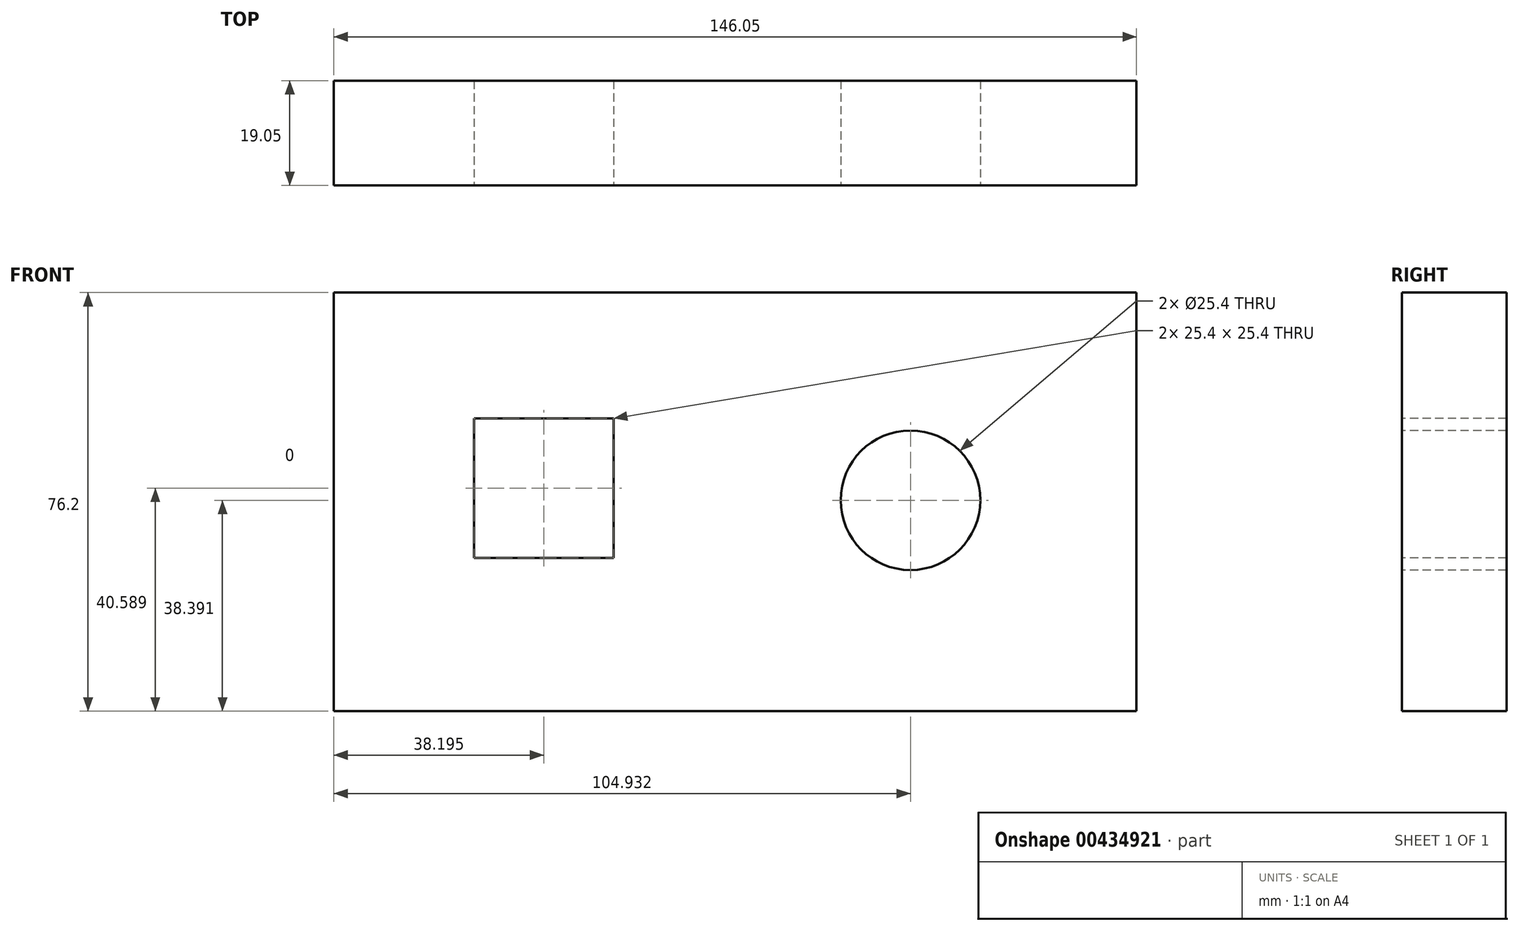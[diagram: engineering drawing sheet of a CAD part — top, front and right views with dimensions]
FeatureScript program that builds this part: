
annotation { "Feature Type Name" : "Feature", "Feature Type Description" : "" }
export const myFeature = defineFeature(function(context is Context, id is Id, definition is map)
    precondition{}
    {
        {
            var Q0;
            Q0=qCreatedBy(makeId("Front.planeOp"),FACE);
            var sketch = newSketch(context, id + "F0", { "sketchPlane" : qUnion([Q0])});
            skLineSegment(sketch, "E0", {"start": v(-76.38, 0) * mm, "end": v(69.67, 0) * mm});
            skLineSegment(sketch, "E1", {"start": v(69.67, 0) * mm, "end": v(69.67, -76.2) * mm});
            skLineSegment(sketch, "E2", {"start": v(69.67, -76.2) * mm, "end": v(-76.38, -76.2) * mm});
            skLineSegment(sketch, "E3", {"start": v(-76.38, -76.2) * mm, "end": v(-76.38, 0) * mm});
            skSolve(sketch);
        }
        {
            var Q0;
            Q0=makeQuery(id+"F0.imprint","IMPRINT",FACE,{"disambiguationData":[TD([[makeQuery(id+"F0.imprint","IMPRINT",EDGE,{"derivedFrom":sQuery(id+"F0.wireOp",EDGE,"E0")}),-1.0]])]});
            extrude(context, id + "F1", {"entities" : qUnion([Q0]), "depth" : 19.05 * mm});
        }
        {
            var Q0;
            Q0=makeQuery(id+"F1.opExtrude","CAP_FACE",FACE,{"disambiguationData":[OSD([sQuery(id+"F0.wireOp",EDGE,"E0"),sQuery(id+"F0.wireOp",EDGE,"E1"),sQuery(id+"F0.wireOp",EDGE,"E2"),sQuery(id+"F0.wireOp",EDGE,"E3")])],"isStart":false});
            var sketch = newSketch(context, id + "F2", { "sketchPlane" : qUnion([Q0])});
            skLineSegment(sketch, "E4", {"start": v(-50.88, -22.91) * mm, "end": v(-50.88, -48.31) * mm});
            skLineSegment(sketch, "E5", {"start": v(-50.88, -48.31) * mm, "end": v(-25.48, -48.31) * mm});
            skLineSegment(sketch, "E6", {"start": v(-25.48, -48.31) * mm, "end": v(-25.48, -22.91) * mm});
            skLineSegment(sketch, "E7", {"start": v(-25.48, -22.91) * mm, "end": v(-50.88, -22.91) * mm});
            skCircle(sketch, "E8", {"center": v(28.55, -37.8) * mm, "radius": 12.7 * mm});
            skSolve(sketch);
        }
        {
            var Q0;
            Q0=makeQuery(id+"F2.imprint","IMPRINT",FACE,{"disambiguationData":[TD([[makeQuery(id+"F2.imprint","IMPRINT",EDGE,{"derivedFrom":sQuery(id+"F2.wireOp",EDGE,"E4")}),1.0]])]});
            var Q1;
            Q1=makeQuery(id+"F2.imprint","IMPRINT",FACE,{"disambiguationData":[TD([[makeQuery(id+"F2.imprint","IMPRINT",EDGE,{"derivedFrom":sQuery(id+"F2.wireOp",EDGE,"E8")}),1.0]])]});
            extrude(context, id + "F3", {"entities" : qUnion([Q0, Q1]), "operationType" : NewBodyOperationType.REMOVE, "oppositeDirection" : true, "depth" : 25.4 * mm});
        }
    });
